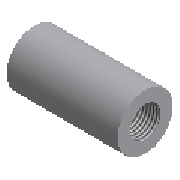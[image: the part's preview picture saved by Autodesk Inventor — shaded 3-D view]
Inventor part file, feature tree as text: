
AUTODESK INVENTOR PART (.ipt)
format: ipt  version: 2025 (Build 290162000, 162)  size: 203,264 bytes
history: native  units: mm (DEFAULTED — no unit token found)
features: other x6, thread x2, revolve x1
ambient origin geometry x8: Origin, YZ Plane, XZ Plane, XY Plane, X Axis, Y Axis, Z Axis, Center Point
bodies: Solid1 (feature_tree)
feature tree (9):
  revolve  "Revolve1"  Angle=90.0deg
  thread  "Thread1"  [1 undecoded]
  thread  "Thread2"  [1 undecoded]
  other  "Work Point1"
  other  "Work Point2"
  other  "Work Axis1"
  other  "Work Point3"
  other  "Work Axis2"
  other  "Work Point4"
note: 2 required parameter values undecoded (feature->parameter linkage not recoverable at this tier; creation-order binding heuristic only, values carry confidence <= 0.55)
